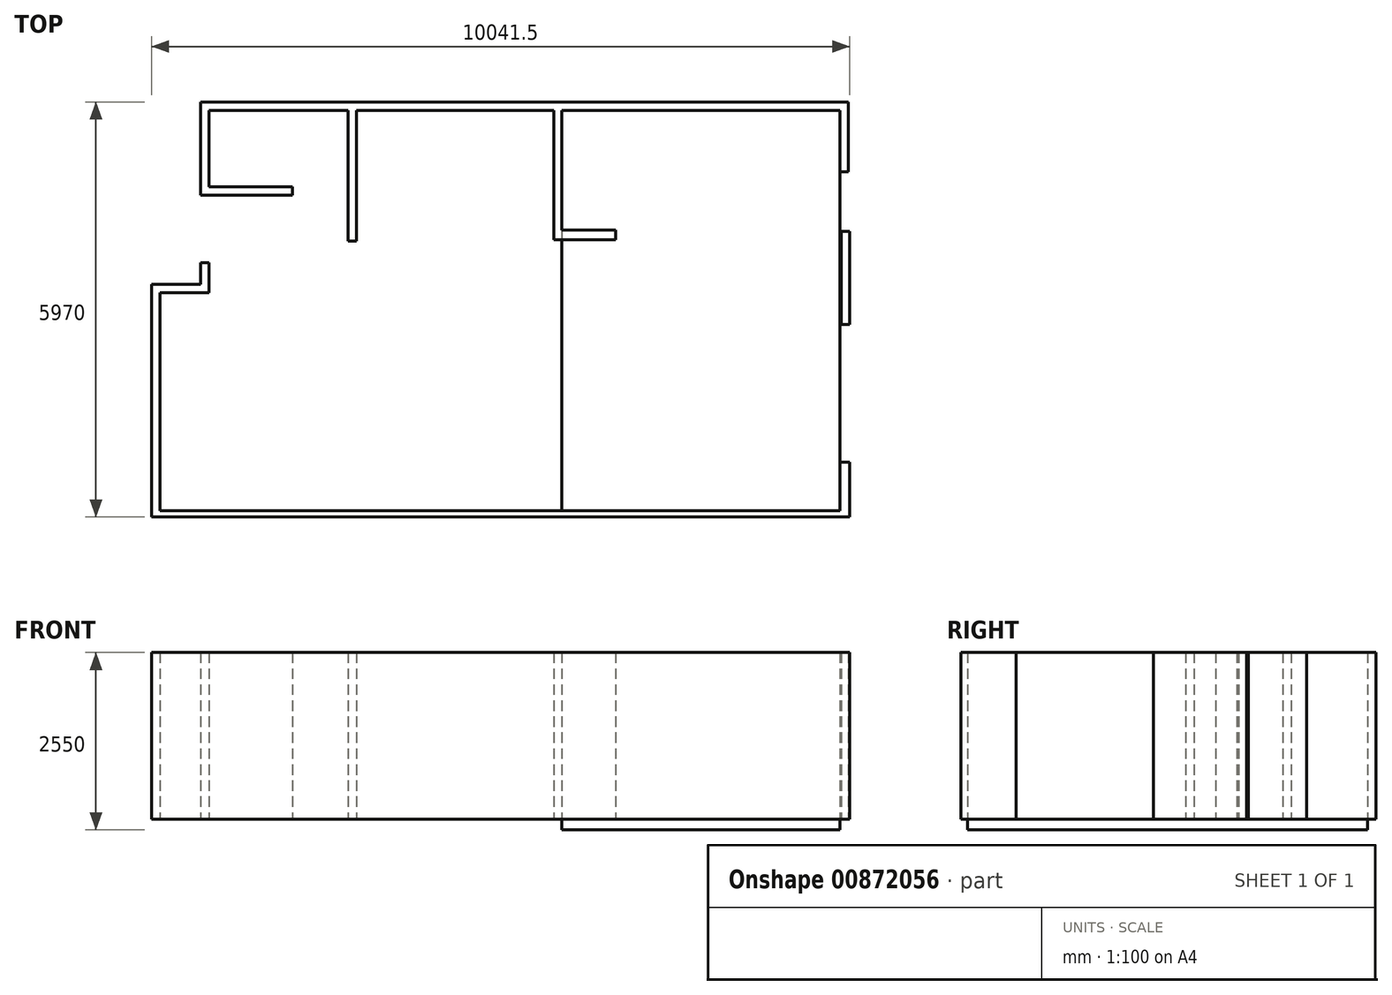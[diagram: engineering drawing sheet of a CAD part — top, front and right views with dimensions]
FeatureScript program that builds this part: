
annotation { "Feature Type Name" : "Feature", "Feature Type Description" : "" }
export const myFeature = defineFeature(function(context is Context, id is Id, definition is map)
    precondition{}
    {
        {
            var Q0;
            Q0=qCreatedBy(makeId("Top.planeOp"),FACE);
            var sketch = newSketch(context, id + "F0", { "sketchPlane" : qUnion([Q0])});
            skLineSegment(sketch, "E0", {"start": v(0, 0) * mm, "end": v(21000, 0) * mm, "construction": true});
            skLineSegment(sketch, "E1", {"start": v(11408.87, -112.07) * mm, "end": v(11408.87, -1892.8) * mm});
            skLineSegment(sketch, "E2", {"start": v(11408.87, -1892.8) * mm, "end": v(12155.09, -1892.8) * mm});
            skLineSegment(sketch, "E3", {"start": v(12155.09, -1892.8) * mm, "end": v(12155.09, -2020) * mm});
            skLineSegment(sketch, "E4", {"start": v(12155.09, -2020) * mm, "end": v(11264.72, -2020) * mm});
            skLineSegment(sketch, "E5", {"start": v(11264.72, -2020) * mm, "end": v(11264.72, -112.07) * mm});
            skLineSegment(sketch, "E6", {"start": v(11264.72, -112.07) * mm, "end": v(8430.92, -112.07) * mm});
            skLineSegment(sketch, "E7", {"start": v(8430.92, -112.07) * mm, "end": v(8430.92, -1993.76) * mm});
            skLineSegment(sketch, "E8", {"start": v(8430.92, -1993.76) * mm, "end": v(8288.3, -1993.76) * mm});
            skLineSegment(sketch, "E9", {"start": v(8288.3, -1993.76) * mm, "end": v(8288.3, -112.07) * mm});
            skLineSegment(sketch, "E10", {"start": v(8288.3, -112.07) * mm, "end": v(6302.23, -112.07) * mm});
            skLineSegment(sketch, "E11", {"start": v(6302.23, -112.07) * mm, "end": v(6302.23, -1232.23) * mm});
            skLineSegment(sketch, "E12", {"start": v(6302.23, -1232.23) * mm, "end": v(7507.29, -1232.23) * mm});
            skLineSegment(sketch, "E13", {"start": v(7507.29, -1232.23) * mm, "end": v(7507.29, -1353.24) * mm});
            skLineSegment(sketch, "E14", {"start": v(7507.29, -1353.24) * mm, "end": v(6181.22, -1353.24) * mm});
            skLineSegment(sketch, "E15", {"start": v(15518.59, -992.12) * mm, "end": v(15386.67, -992.12) * mm});
            skLineSegment(sketch, "E16", {"start": v(15386.67, -992.12) * mm, "end": v(15386.67, -112.07) * mm});
            skLineSegment(sketch, "E17", {"start": v(15518.59, -992.12) * mm, "end": v(15518.59, 0) * mm});
            skLineSegment(sketch, "E18.bottom", {"start": v(15512.16, -3210.92) * mm, "end": v(15380.25, -3210.92) * mm});
            skLineSegment(sketch, "E18.top", {"start": v(15512.16, -1866.8) * mm, "end": v(15380.25, -1866.8) * mm});
            skLineSegment(sketch, "E18.left", {"start": v(15512.16, -3210.92) * mm, "end": v(15512.16, -1866.8) * mm});
            skLineSegment(sketch, "E18.right", {"start": v(15380.25, -3210.92) * mm, "end": v(15380.25, -1866.8) * mm});
            skLineSegment(sketch, "E19", {"start": v(15499.43, -5194.69) * mm, "end": v(15499.43, -5998.9) * mm});
            skLineSegment(sketch, "E20", {"start": v(15499.43, -5998.9) * mm, "end": v(5468.29, -5998.9) * mm});
            skLineSegment(sketch, "E21", {"start": v(5468.29, -5998.9) * mm, "end": v(5468.29, -2605.2) * mm});
            skLineSegment(sketch, "E22", {"start": v(5468.29, -2605.2) * mm, "end": v(6177.08, -2605.2) * mm});
            skLineSegment(sketch, "E23", {"start": v(6177.08, -2605.2) * mm, "end": v(6177.08, -2304.99) * mm});
            skLineSegment(sketch, "E24", {"start": v(6177.08, -2304.99) * mm, "end": v(6302.37, -2304.99) * mm});
            skLineSegment(sketch, "E25", {"start": v(6302.37, -2304.99) * mm, "end": v(6302.37, -2729.25) * mm});
            skLineSegment(sketch, "E26", {"start": v(6302.37, -2729.25) * mm, "end": v(5610.7, -2729.25) * mm});
            skLineSegment(sketch, "E27", {"start": v(5610.7, -2729.25) * mm, "end": v(5610.7, -5844.52) * mm});
            skLineSegment(sketch, "E28", {"start": v(5610.7, -5844.52) * mm, "end": v(15371.72, -5844.52) * mm});
            skLineSegment(sketch, "E29", {"start": v(15371.72, -5844.52) * mm, "end": v(15371.72, -5194.69) * mm});
            skLineSegment(sketch, "E30", {"start": v(15371.72, -5194.69) * mm, "end": v(15499.43, -5194.69) * mm});
            skLineSegment(sketch, "E31", {"start": v(6181.22, -1353.24) * mm, "end": v(6177.08, 0) * mm});
            skPoint(sketch, "E32", {"position": v(0, 0) * mm});
            skLineSegment(sketch, "E33", {"start": v(11408.87, -112.07) * mm, "end": v(15386.67, -112.07) * mm});
            skLineSegment(sketch, "E34", {"start": v(6177.08, 0) * mm, "end": v(15518.59, 0) * mm});
            skSolve(sketch);
        }
        {
            var Q0;
            Q0=qCreatedBy(makeId("Top.planeOp"),FACE);
            var sketch = newSketch(context, id + "F1", { "sketchPlane" : qUnion([Q0])});
            skLineSegment(sketch, "E35", {"start": v(0, 0) * mm, "end": v(21000, 0) * mm, "construction": true});
            skLineSegment(sketch, "E36", {"start": v(11380, -120) * mm, "end": v(11380, -1840) * mm});
            skLineSegment(sketch, "E37", {"start": v(11380, -1840) * mm, "end": v(12150, -1840) * mm});
            skLineSegment(sketch, "E38", {"start": v(12150, -1840) * mm, "end": v(12150, -1980) * mm});
            skLineSegment(sketch, "E39", {"start": v(12150, -1980) * mm, "end": v(11260, -1980) * mm});
            skLineSegment(sketch, "E40", {"start": v(11260, -1980) * mm, "end": v(11260, -120) * mm});
            skLineSegment(sketch, "E41", {"start": v(11260, -120) * mm, "end": v(8424.72, -120) * mm});
            skLineSegment(sketch, "E42", {"start": v(8424.72, -120) * mm, "end": v(8424.72, -2000) * mm});
            skLineSegment(sketch, "E43", {"start": v(8424.72, -2000) * mm, "end": v(8304.72, -2000) * mm});
            skLineSegment(sketch, "E44", {"start": v(8304.72, -2000) * mm, "end": v(8304.72, -120) * mm});
            skLineSegment(sketch, "E45", {"start": v(8304.72, -120) * mm, "end": v(6304.72, -120) * mm});
            skLineSegment(sketch, "E46", {"start": v(6304.72, -120) * mm, "end": v(6304.72, -1220) * mm});
            skLineSegment(sketch, "E47", {"start": v(6304.72, -1220) * mm, "end": v(7504.72, -1220) * mm});
            skLineSegment(sketch, "E48", {"start": v(7504.72, -1220) * mm, "end": v(7504.72, -1340) * mm});
            skLineSegment(sketch, "E49", {"start": v(7504.72, -1340) * mm, "end": v(6184.72, -1340) * mm});
            skLineSegment(sketch, "E50", {"start": v(15500, -1000) * mm, "end": v(15380, -1000) * mm});
            skLineSegment(sketch, "E51", {"start": v(15380, -1000) * mm, "end": v(15380, -120) * mm});
            skLineSegment(sketch, "E52", {"start": v(15500, -1000) * mm, "end": v(15500, 0) * mm});
            skLineSegment(sketch, "E53.bottom", {"start": v(15518.59, -3200) * mm, "end": v(15398.59, -3200) * mm});
            skLineSegment(sketch, "E53.top", {"start": v(15518.59, -1860) * mm, "end": v(15398.59, -1860) * mm});
            skLineSegment(sketch, "E53.left", {"start": v(15518.59, -3200) * mm, "end": v(15518.59, -1860) * mm});
            skLineSegment(sketch, "E53.right", {"start": v(15398.59, -3200) * mm, "end": v(15398.59, -1860) * mm});
            skLineSegment(sketch, "E54", {"start": v(15518.59, -5180) * mm, "end": v(15518.59, -5970) * mm});
            skLineSegment(sketch, "E55", {"start": v(15518.59, -5970) * mm, "end": v(5477.08, -5970) * mm});
            skLineSegment(sketch, "E56", {"start": v(5477.08, -5970) * mm, "end": v(5477.08, -2620) * mm});
            skLineSegment(sketch, "E57", {"start": v(5477.08, -2620) * mm, "end": v(6184.72, -2620) * mm});
            skLineSegment(sketch, "E58", {"start": v(6184.72, -2620) * mm, "end": v(6184.72, -2310) * mm});
            skLineSegment(sketch, "E59", {"start": v(6184.72, -2310) * mm, "end": v(6304.72, -2310) * mm});
            skLineSegment(sketch, "E60", {"start": v(6304.72, -2310) * mm, "end": v(6304.72, -2740) * mm});
            skLineSegment(sketch, "E61", {"start": v(6304.72, -2740) * mm, "end": v(5597.08, -2740) * mm});
            skLineSegment(sketch, "E62", {"start": v(5597.08, -2740) * mm, "end": v(5597.08, -5878.9) * mm});
            skLineSegment(sketch, "E63", {"start": v(5597.08, -5878.9) * mm, "end": v(15380.25, -5878.9) * mm});
            skLineSegment(sketch, "E64", {"start": v(15380.25, -5878.9) * mm, "end": v(15380.25, -5180) * mm});
            skLineSegment(sketch, "E65", {"start": v(15380.25, -5180) * mm, "end": v(15518.59, -5180) * mm});
            skLineSegment(sketch, "E66", {"start": v(6184.72, -1340) * mm, "end": v(6184.72, 0) * mm});
            skPoint(sketch, "E67", {"position": v(0, 0) * mm});
            skLineSegment(sketch, "E68", {"start": v(11380, -120) * mm, "end": v(15380, -120) * mm});
            skLineSegment(sketch, "E69", {"start": v(6184.72, 0) * mm, "end": v(15500, 0) * mm});
            skLineSegment(sketch, "E70", {"start": v(11260, -120) * mm, "end": v(11380, -120) * mm, "construction": true});
            skPoint(sketch, "E71", {"position": v(11320, -120) * mm});
            skPoint(sketch, "E72", {"position": v(15440, -1000) * mm});
            skLineSegment(sketch, "E73", {"start": v(8304.72, -120) * mm, "end": v(8424.72, -120) * mm, "construction": true});
            skPoint(sketch, "E74", {"position": v(8364.72, -120) * mm});
            skSolve(sketch);
        }
        {
            var Q0;
            Q0=qSketchRegion(id+"F1",true);
            extrude(context, id + "F2", {"entities" : qUnion([Q0]), "depth" : 2400 * mm, "offsetDistance" : 25 * mm});
        }
        {
            var Q0;
            Q0=qCreatedBy(makeId("Top.planeOp"),FACE);
            var sketch = newSketch(context, id + "F3", { "sketchPlane" : qUnion([Q0])});
            skLineSegment(sketch, "E75.0", {"start": v(11380, -120) * mm, "end": v(11380, -5878.9) * mm});
            skLineSegment(sketch, "E75.2", {"start": v(11380, -120) * mm, "end": v(15380, -120) * mm});
            skLineSegment(sketch, "E76.0", {"start": v(11380, -5878.9) * mm, "end": v(15380.25, -5878.9) * mm});
            skLineSegment(sketch, "E77", {"start": v(15380.25, -5878.9) * mm, "end": v(15380, -120) * mm});
            skSolve(sketch);
        }
        {
            var Q0;
            Q0=makeQuery(id+"F3.imprint","IMPRINT",FACE,{"disambiguationData":[TD([[makeQuery(id+"F3.imprint","IMPRINT",EDGE,{"derivedFrom":sQuery(id+"F3.wireOp",EDGE,"E75.0")}),1.0]])]});
            extrude(context, id + "F4", {"entities" : qUnion([Q0]), "oppositeDirection" : true, "depth" : 150 * mm, "offsetDistance" : 25 * mm});
        }
    });
